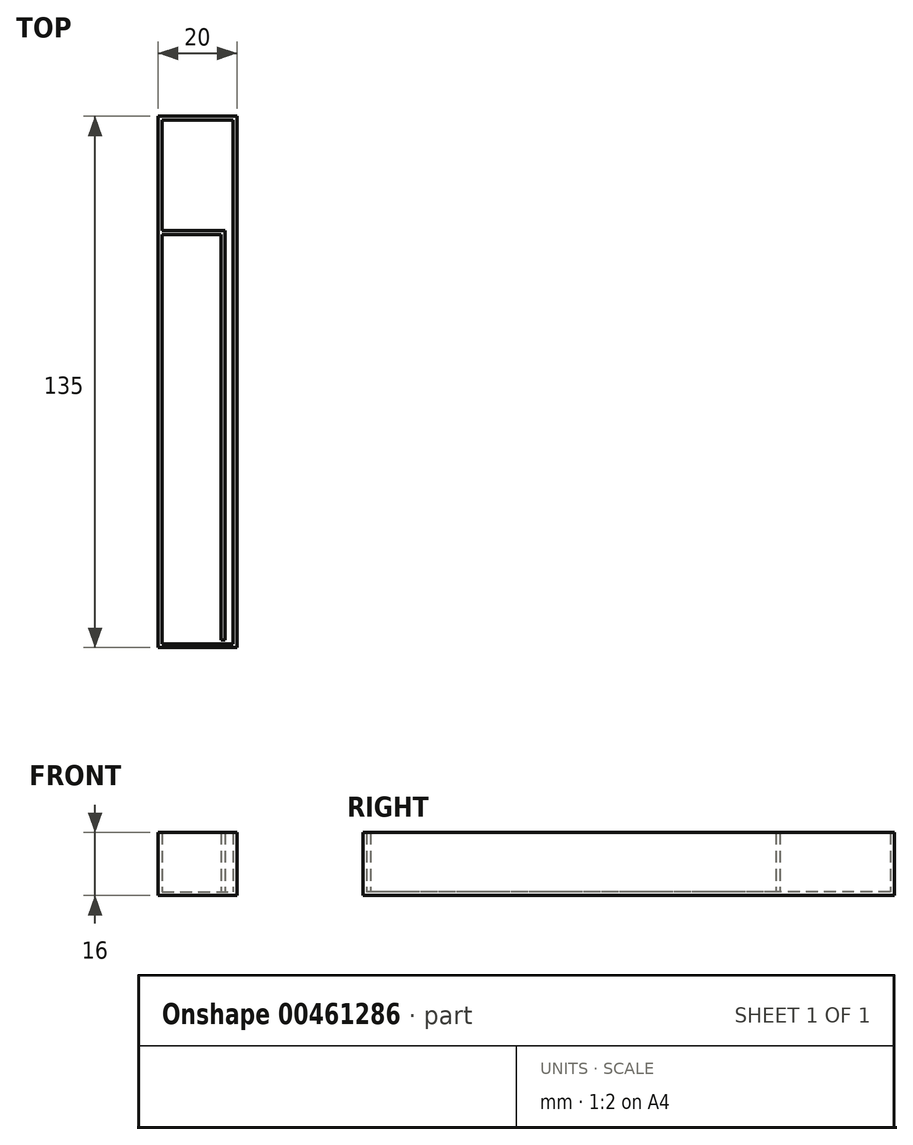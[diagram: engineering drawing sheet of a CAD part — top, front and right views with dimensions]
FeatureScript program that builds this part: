
annotation { "Feature Type Name" : "Feature", "Feature Type Description" : "" }
export const myFeature = defineFeature(function(context is Context, id is Id, definition is map)
    precondition{}
    {
        {
            var Q0;
            Q0=qCreatedBy(makeId("Top.planeOp"),FACE);
            var sketch = newSketch(context, id + "F0", { "sketchPlane" : qUnion([Q0])});
            skLineSegment(sketch, "E0.bottom", {"start": v(-10, 67.5) * mm, "end": v(10, 67.5) * mm});
            skLineSegment(sketch, "E0.top", {"start": v(-10, -67.5) * mm, "end": v(10, -67.5) * mm});
            skLineSegment(sketch, "E0.left", {"start": v(-10, 67.5) * mm, "end": v(-10, -67.5) * mm});
            skLineSegment(sketch, "E0.right", {"start": v(10, 67.5) * mm, "end": v(10, -67.5) * mm});
            skPoint(sketch, "E0.middle", {"position": v(0, 0) * mm});
            skSolve(sketch);
        }
        {
            var Q0;
            Q0 = qSketchRegion(id + "F0", true);
            extrude(context, id + "F1", {"entities" : qUnion([Q0]), "depth" : 1 * mm});
        }
        {
            var Q0;
            Q0=makeQuery(id+"F1.opExtrude","CAP_FACE",FACE,{"disambiguationData":[OSD([sQuery(id+"F0.wireOp",EDGE,"E0.bottom"),sQuery(id+"F0.wireOp",EDGE,"E0.top"),sQuery(id+"F0.wireOp",EDGE,"E0.left"),sQuery(id+"F0.wireOp",EDGE,"E0.right")])],"isStart":false});
            var sketch = newSketch(context, id + "F2", { "sketchPlane" : qUnion([Q0])});
            skLineSegment(sketch, "E1.bottom", {"start": v(-10, -67.5) * mm, "end": v(10, -67.5) * mm});
            skLineSegment(sketch, "E1.top", {"start": v(-10, -66.5) * mm, "end": v(10, -66.5) * mm});
            skLineSegment(sketch, "E1.left", {"start": v(-10, -67.5) * mm, "end": v(-10, -66.5) * mm});
            skLineSegment(sketch, "E1.right", {"start": v(10, -67.5) * mm, "end": v(10, -66.5) * mm});
            skLineSegment(sketch, "E2.bottom", {"start": v(-10, 67.5) * mm, "end": v(-9, 67.5) * mm});
            skLineSegment(sketch, "E2.top", {"start": v(-10, -66.5) * mm, "end": v(-9, -66.5) * mm});
            skLineSegment(sketch, "E2.left", {"start": v(-10, 67.5) * mm, "end": v(-10, -66.5) * mm});
            skLineSegment(sketch, "E2.right", {"start": v(-9, 67.5) * mm, "end": v(-9, -66.5) * mm});
            skLineSegment(sketch, "E3.bottom", {"start": v(10, 67.5) * mm, "end": v(9, 67.5) * mm});
            skLineSegment(sketch, "E3.top", {"start": v(10, -66.5) * mm, "end": v(9, -66.5) * mm});
            skLineSegment(sketch, "E3.left", {"start": v(10, 67.5) * mm, "end": v(10, -66.5) * mm});
            skLineSegment(sketch, "E3.right", {"start": v(9, 67.5) * mm, "end": v(9, -66.5) * mm});
            skLineSegment(sketch, "E4.bottom", {"start": v(-9, 66.5) * mm, "end": v(9, 66.5) * mm});
            skLineSegment(sketch, "E4.top", {"start": v(-9, 67.5) * mm, "end": v(9, 67.5) * mm});
            skLineSegment(sketch, "E4.left", {"start": v(-9, 66.5) * mm, "end": v(-9, 67.5) * mm});
            skLineSegment(sketch, "E4.right", {"start": v(9, 66.5) * mm, "end": v(9, 67.5) * mm});
            skLineSegment(sketch, "E5.bottom", {"start": v(-9, 37.5) * mm, "end": v(6, 37.5) * mm});
            skLineSegment(sketch, "E5.top", {"start": v(-9, 38.5) * mm, "end": v(7, 38.5) * mm});
            skLineSegment(sketch, "E5.left", {"start": v(-9, 38.5) * mm, "end": v(-9, 37.5) * mm});
            skLineSegment(sketch, "E6.top", {"start": v(6, -65.5) * mm, "end": v(7, -65.5) * mm});
            skLineSegment(sketch, "E6.left", {"start": v(6, 37.5) * mm, "end": v(6, -65.5) * mm});
            skLineSegment(sketch, "E6.right", {"start": v(7, 38.5) * mm, "end": v(7, -65.5) * mm});
            skSolve(sketch);
        }
        {
            var Q0;
            Q0 = qSketchRegion(id + "F2", true);
            var Q1;
            Q1=makeQuery(id+"F2.imprint","IMPRINT",FACE,{"disambiguationData":[TD([[makeQuery(id+"F2.imprint","IMPRINT",EDGE,{"derivedFrom":sQuery(id+"F2.wireOp",EDGE,"E5.bottom")}),1.0]])]});
            extrude(context, id + "F3", {"entities" : qUnion([Q0, Q1]), "operationType" : NewBodyOperationType.ADD, "depth" : 15 * mm});
        }
    });
